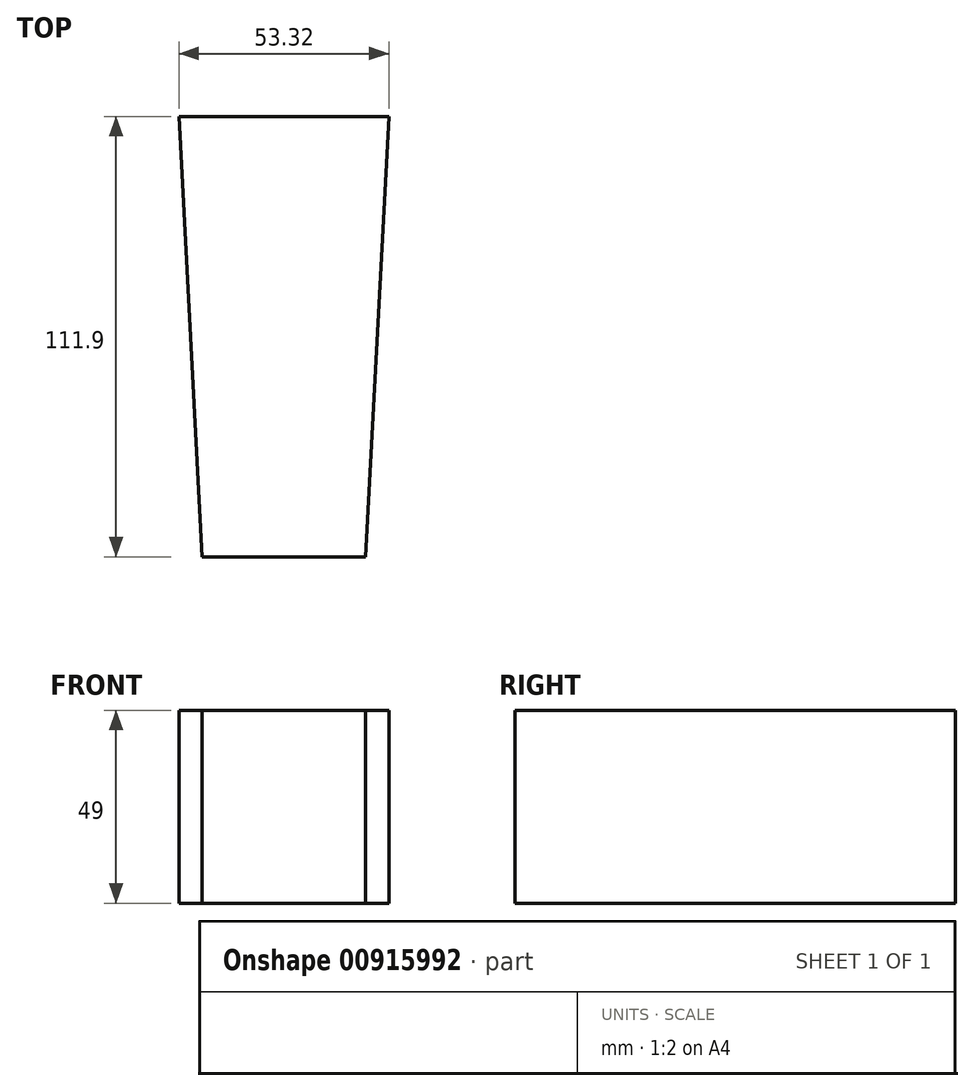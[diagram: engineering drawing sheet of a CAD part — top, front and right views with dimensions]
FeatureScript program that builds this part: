
annotation { "Feature Type Name" : "Feature", "Feature Type Description" : "" }
export const myFeature = defineFeature(function(context is Context, id is Id, definition is map)
    precondition{}
    {
        {
            var Q0;
            Q0=qCreatedBy(makeId("Top.planeOp"),FACE);
            var sketch = newSketch(context, id + "F0", { "sketchPlane" : qUnion([Q0])});
            skLineSegment(sketch, "E0.bottom", {"start": v(-26.86, 40.59) * mm, "end": v(26.46, 40.59) * mm});
            skLineSegment(sketch, "E0.top", {"start": v(-21, -71.31) * mm, "end": v(20.6, -71.31) * mm});
            skLineSegment(sketch, "E1.bottom", {"start": v(-21, 40.59) * mm, "end": v(20.6, 40.59) * mm});
            skLineSegment(sketch, "E2", {"start": v(-26.86, 40.59) * mm, "end": v(-21, -71.31) * mm});
            skLineSegment(sketch, "E3", {"start": v(26.46, 40.59) * mm, "end": v(20.6, -71.31) * mm});
            skSolve(sketch);
        }
        {
            var Q0;
            Q0 = qSketchRegion(id + "F0", true);
            extrude(context, id + "F1", {"entities" : qUnion([Q0]), "depth" : 49 * mm, "offsetDistance" : 25 * mm});
        }
    });
